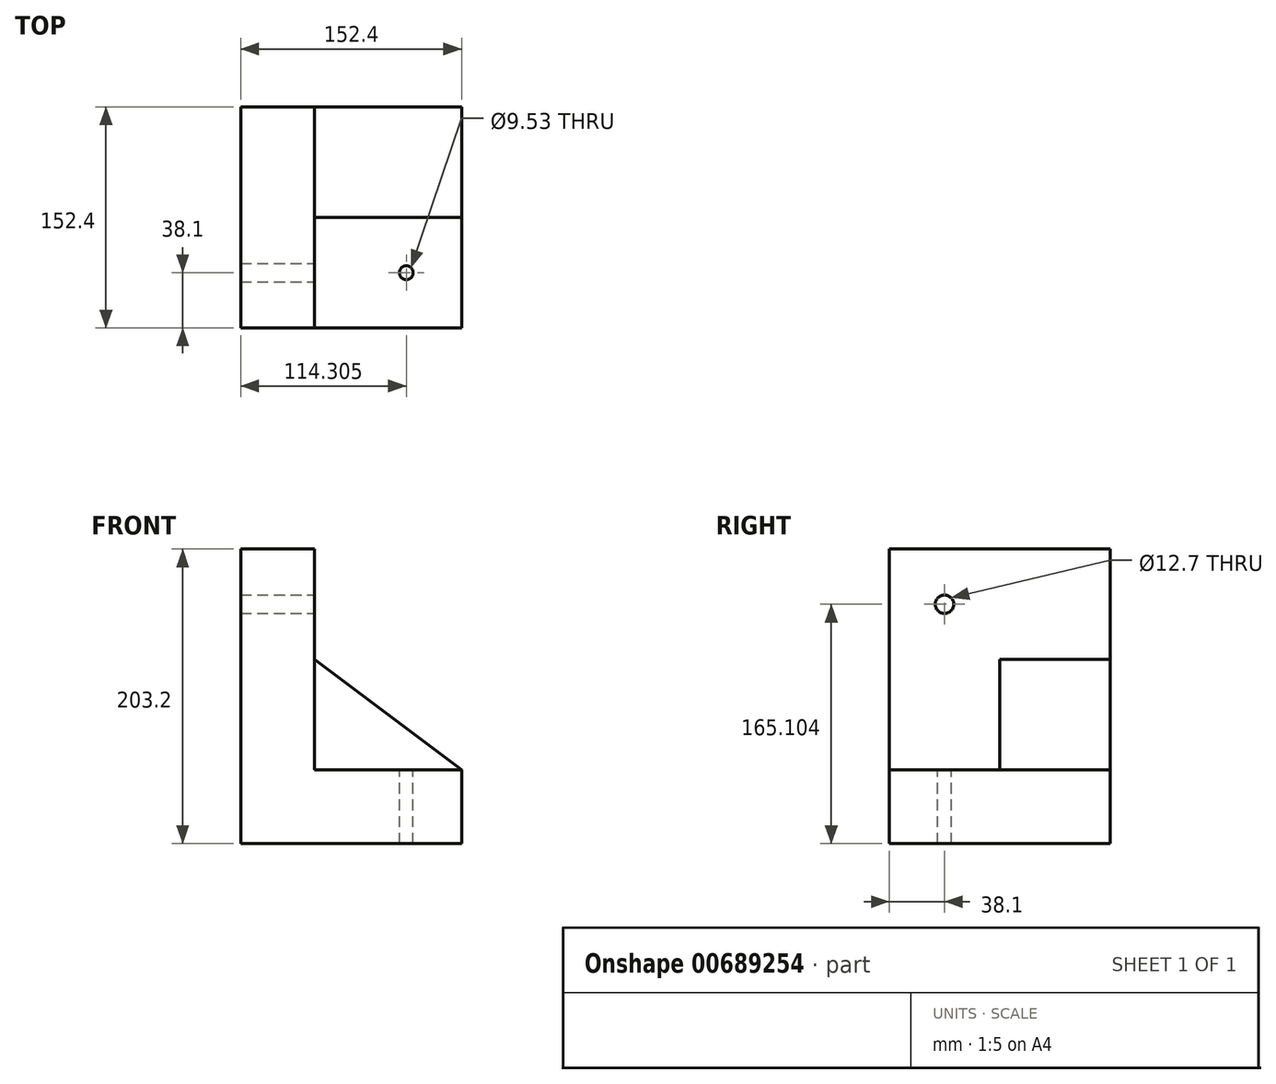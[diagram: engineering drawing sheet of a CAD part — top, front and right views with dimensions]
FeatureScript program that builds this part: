
annotation { "Feature Type Name" : "Feature", "Feature Type Description" : "" }
export const myFeature = defineFeature(function(context is Context, id is Id, definition is map)
    precondition{}
    {
        {
            var Q0;
            Q0=qCreatedBy(makeId("Front.planeOp"),FACE);
            var sketch = newSketch(context, id + "F0", { "sketchPlane" : qUnion([Q0])});
            skLineSegment(sketch, "E0", {"start": v(-66.09, 141.98) * mm, "end": v(-15.29, 141.98) * mm});
            skLineSegment(sketch, "E1", {"start": v(-15.29, 141.98) * mm, "end": v(-66.09, 141.98) * mm});
            skLineSegment(sketch, "E2", {"start": v(-66.09, -61.22) * mm, "end": v(-66.09, 141.98) * mm});
            skLineSegment(sketch, "E3", {"start": v(-66.09, -61.22) * mm, "end": v(86.31, -61.22) * mm});
            skLineSegment(sketch, "E4", {"start": v(86.31, -61.22) * mm, "end": v(86.31, -10.42) * mm});
            skLineSegment(sketch, "E5", {"start": v(86.31, -10.42) * mm, "end": v(-15.29, -10.42) * mm});
            skLineSegment(sketch, "E6", {"start": v(-15.29, -10.42) * mm, "end": v(-15.29, 141.98) * mm});
            skSolve(sketch);
        }
        {
            var Q0;
            Q0 = qSketchRegion(id + "F0", true);
            extrude(context, id + "F1", {"entities" : qUnion([Q0]), "depth" : 152.4 * mm, "offsetDistance" : 25.4 * mm});
        }
        {
            var Q0;
            Q0=makeQuery(id+"F1.opExtrude","SWEPT_FACE",FACE,{"disambiguationData":[OSD([sQuery(id+"F0.wireOp",EDGE,"E5")])]});
            var sketch = newSketch(context, id + "F2", { "sketchPlane" : qUnion([Q0])});
            skLineSegment(sketch, "E7.bottom", {"start": v(-15.29, 0) * mm, "end": v(86.31, 0) * mm});
            skLineSegment(sketch, "E7.top", {"start": v(-15.29, -76.2) * mm, "end": v(86.31, -76.2) * mm});
            skLineSegment(sketch, "E7.left", {"start": v(-15.29, 0) * mm, "end": v(-15.29, -76.2) * mm});
            skLineSegment(sketch, "E7.right", {"start": v(86.31, 0) * mm, "end": v(86.31, -76.2) * mm});
            skSolve(sketch);
        }
        {
            var Q0;
            Q0 = qSketchRegion(id + "F2", true);
            extrude(context, id + "F3", {"entities" : qUnion([Q0]), "operationType" : NewBodyOperationType.ADD, "depth" : 76.2 * mm, "offsetDistance" : 25.4 * mm});
        }
        {
            var Q0;
            Q0=makeQuery(id+"F3.opExtrude","SWEPT_FACE",FACE,{"disambiguationData":[OSD([sQuery(id+"F2.wireOp",EDGE,"E7.top")])]});
            var sketch = newSketch(context, id + "F4", { "sketchPlane" : qUnion([Q0])});
            skLineSegment(sketch, "E8", {"start": v(-15.29, 65.78) * mm, "end": v(86.31, -10.42) * mm});
            skSolve(sketch);
        }
        {
            var Q0;
            Q0=makeQuery(id+"F4.imprint","IMPRINT",FACE,{"disambiguationData":[TD([[makeQuery(id+"F4.imprint","IMPRINT",EDGE,{"derivedFrom":sQuery(id+"F4.wireOp",EDGE,"E8")}),1.0]])]});
            extrude(context, id + "F5", {"entities" : qUnion([Q0]), "operationType" : NewBodyOperationType.REMOVE, "oppositeDirection" : true, "depth" : 76.2 * mm, "offsetDistance" : 25.4 * mm});
        }
        {
            var Q0;
            Q0=makeQuery(id+"F1.opExtrude","SWEPT_FACE",FACE,{"disambiguationData":[OSD([sQuery(id+"F0.wireOp",EDGE,"E5")])]});
            var sketch = newSketch(context, id + "F6", { "sketchPlane" : qUnion([Q0])});
            skCircle(sketch, "E9", {"center": v(48.21, -114.3) * mm, "radius": 4.76 * mm});
            skSolve(sketch);
        }
        {
            var Q0;
            Q0=sQuery(id+"F6.wireOp",VERTEX,"E9.center");
            var Q1;
            Q1=makeQuery(id+"F1.opExtrude","SWEPT_BODY",BODY,{"disambiguationData":[OSD([sQuery(id+"F0.wireOp",EDGE,"E1"),sQuery(id+"F0.wireOp",EDGE,"E2"),sQuery(id+"F0.wireOp",EDGE,"E3"),sQuery(id+"F0.wireOp",EDGE,"E4"),sQuery(id+"F0.wireOp",EDGE,"E5"),sQuery(id+"F0.wireOp",EDGE,"E6")])]});
            hole(context, id + "F7", {"style" : HoleStyle.SIMPLE, "endStyle" : HoleEndStyle.THROUGH, "holeDiameter" : 9.52 * mm, "majorDiameter" : 6.35 * mm, "isTappedThrough" : true, "tappedDepth" : 12.7 * mm, "tapClearance" : 3, "locations" : qUnion([Q0]), "scope" : qUnion([Q1])});
        }
        {
            var Q0;
            Q0=makeQuery(id+"F1.opExtrude","SWEPT_FACE",FACE,{"disambiguationData":[OSD([sQuery(id+"F0.wireOp",EDGE,"E6")])]});
            var sketch = newSketch(context, id + "F8", { "sketchPlane" : qUnion([Q0])});
            skPoint(sketch, "E10", {"position": v(-114.3, 103.88) * mm});
            skSolve(sketch);
        }
        {
            var Q0;
            Q0=sQuery(id+"F8.wireOp",VERTEX,"E10");
            var Q1;
            Q1=makeQuery(id+"F1.opExtrude","SWEPT_BODY",BODY,{"disambiguationData":[OSD([sQuery(id+"F0.wireOp",EDGE,"E1"),sQuery(id+"F0.wireOp",EDGE,"E2"),sQuery(id+"F0.wireOp",EDGE,"E3"),sQuery(id+"F0.wireOp",EDGE,"E4"),sQuery(id+"F0.wireOp",EDGE,"E5"),sQuery(id+"F0.wireOp",EDGE,"E6")])]});
            hole(context, id + "F9", {"style" : HoleStyle.SIMPLE, "endStyle" : HoleEndStyle.THROUGH, "holeDiameter" : 12.7 * mm, "majorDiameter" : 6.35 * mm, "isTappedThrough" : true, "tappedDepth" : 12.7 * mm, "tapClearance" : 3, "locations" : qUnion([Q0]), "scope" : qUnion([Q1])});
        }
    });
